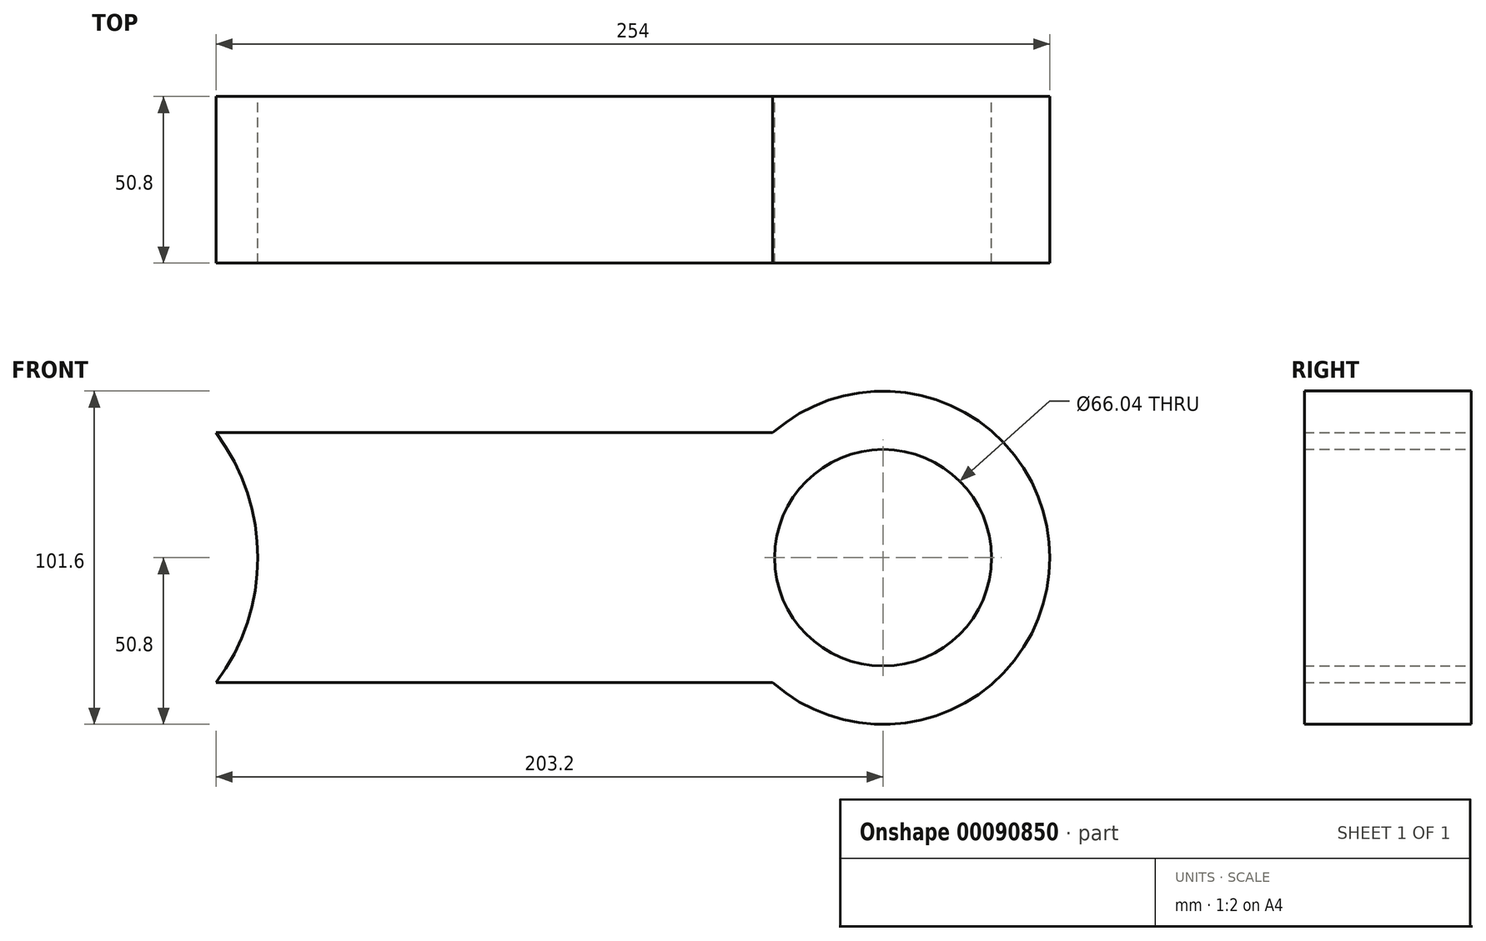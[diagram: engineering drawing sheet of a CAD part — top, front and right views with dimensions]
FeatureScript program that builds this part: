
annotation { "Feature Type Name" : "Feature", "Feature Type Description" : "" }
export const myFeature = defineFeature(function(context is Context, id is Id, definition is map)
    precondition{}
    {
        {
            var Q0;
            Q0=qCreatedBy(makeId("Front.planeOp"),FACE);
            var sketch = newSketch(context, id + "F0", { "sketchPlane" : qUnion([Q0])});
            skCircle(sketch, "E0", {"center": v(0, 0) * mm, "radius": 63.5 * mm});
            skCircle(sketch, "E1", {"center": v(254, 0) * mm, "radius": 50.8 * mm});
            skLineSegment(sketch, "E2", {"start": v(0, 0) * mm, "end": v(254, 0) * mm, "construction": true});
            skLineSegment(sketch, "E3", {"start": v(50.8, 38.1) * mm, "end": v(220.4, 38.1) * mm});
            skLineSegment(sketch, "E4.MirrorCS", {"start": v(50.8, -38.1) * mm, "end": v(220.4, -38.1) * mm});
            skCircle(sketch, "E5", {"center": v(0, 0) * mm, "radius": 33.02 * mm});
            skCircle(sketch, "E6", {"center": v(254, 0) * mm, "radius": 33.02 * mm});
            skSolve(sketch);
        }
        {
            var Q0;
            {var subQ0=sQuery(id+"F0.wireOp",EDGE,"E3");Q0=makeQuery(id+"F0.imprint","IMPRINT",FACE,{"disambiguationData":[TD([[makeQuery(id+"F0.imprint","IMPRINT",EDGE,{"derivedFrom":subQ0}),-1.0]])]});}
            var Q1;
            Q1=makeQuery(id+"F0.imprint","IMPRINT",FACE,{"disambiguationData":[TD([[makeQuery(id+"F0.imprint","IMPRINT",EDGE,{"derivedFrom":sQuery(id+"F0.wireOp",EDGE,"E6")}),-1.0]])]});
            extrude(context, id + "F1", {"entities" : qUnion([Q0, Q1]), "depth" : 50.8 * mm});
        }
    });
